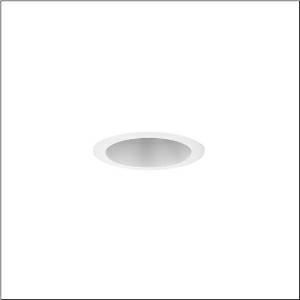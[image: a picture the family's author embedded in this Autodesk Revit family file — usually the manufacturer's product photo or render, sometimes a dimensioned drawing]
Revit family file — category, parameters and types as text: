
# Revit family: lunis_31_mini_51dn16de31
name_source: partatom
category: Lighting Fixtures
units: mm (PartAtom-declared; Revit-internal decimal feet)

## family parameters
Cut with Voids When Loaded = No
Host = Face
Light Source = No
Part Type = Normal
Room Calculation Point = No
Round Connector Dimension = Use Diameter
Shared = No

## types (1)
- Lunis 31 mini (1 x LED, 1000 lm, 8.3 W, 3000K)
    Apparent Load = 8 VA
    CIE Flux Codes = 69 93 99 100 100
    Color Rendering = 80
    Color Temperature = 3000K
    Default Elevation = 1800 mm
    Description = Lunis 31,  mini, downlight, light control with reflector, light emission: direct distribution, LED rated luminous flux: 1.000lm, light colour: 830, mains connection: 220..240V, AC, 50/60Hz, housing, white, protection rating (complete): IP20, protection rating (on room side): IP54, insulation class (complete): insulation class II (safety insulation), certification: CE, packaging unit: 1 piece
    Height = 0 mm  [stored 0 ft]
    Lamp = 1 x LED
    Lamp Light Flux = 1000 lm
    Lamp Power = 8.3 W
    Lamp count = 1
    Length = 188 mm  [stored 0.616798 ft]
    Luminous efficacy = 120 lm/W
    Manufacturer = Siteco
    ModVariant = No
    Model = 51DN16DE31
    Mounting Place = Ceiling
    Mounting Type = Recessed
    Number of Poles = 1
    OnlyDefault = Yes
    Power Factor = 1
    Product Name = Lunis 31 mini
    Product group = downlight
    ProductGroupID = 401
    Protection Class = Protection class II
    Protection Degree = IP 20
    RLX_Detail_Level = 1
    RLX_Emergency_Light_Flux = 0 lm
    RLX_Emergency_Type = 0
    RLX_Emergency_Type_DB = No
    RlxData = <blob elided: 21821 chars, md5=61783e39>
    Socket = socket
    Standby Power = 0 W
    System Light Flux = 1000 lm
    System Power = 8 W
    Type Comments = Product without accessories
    Type Image = l_1345911.jpg
    URL = http://relux.com
    VarID = ---
    Voltage = 0 V
    Weight = 0.00 kg
    Width = 0 mm  [stored 0 ft]

note: [stored X ft] marks values corroborated as IEEE doubles in the binary element streams (Revit-internal decimal feet)

## geometry (parser evidence)
native form markers: Blend x4, Sweep x13
no freeform markers — native parametric forms only
